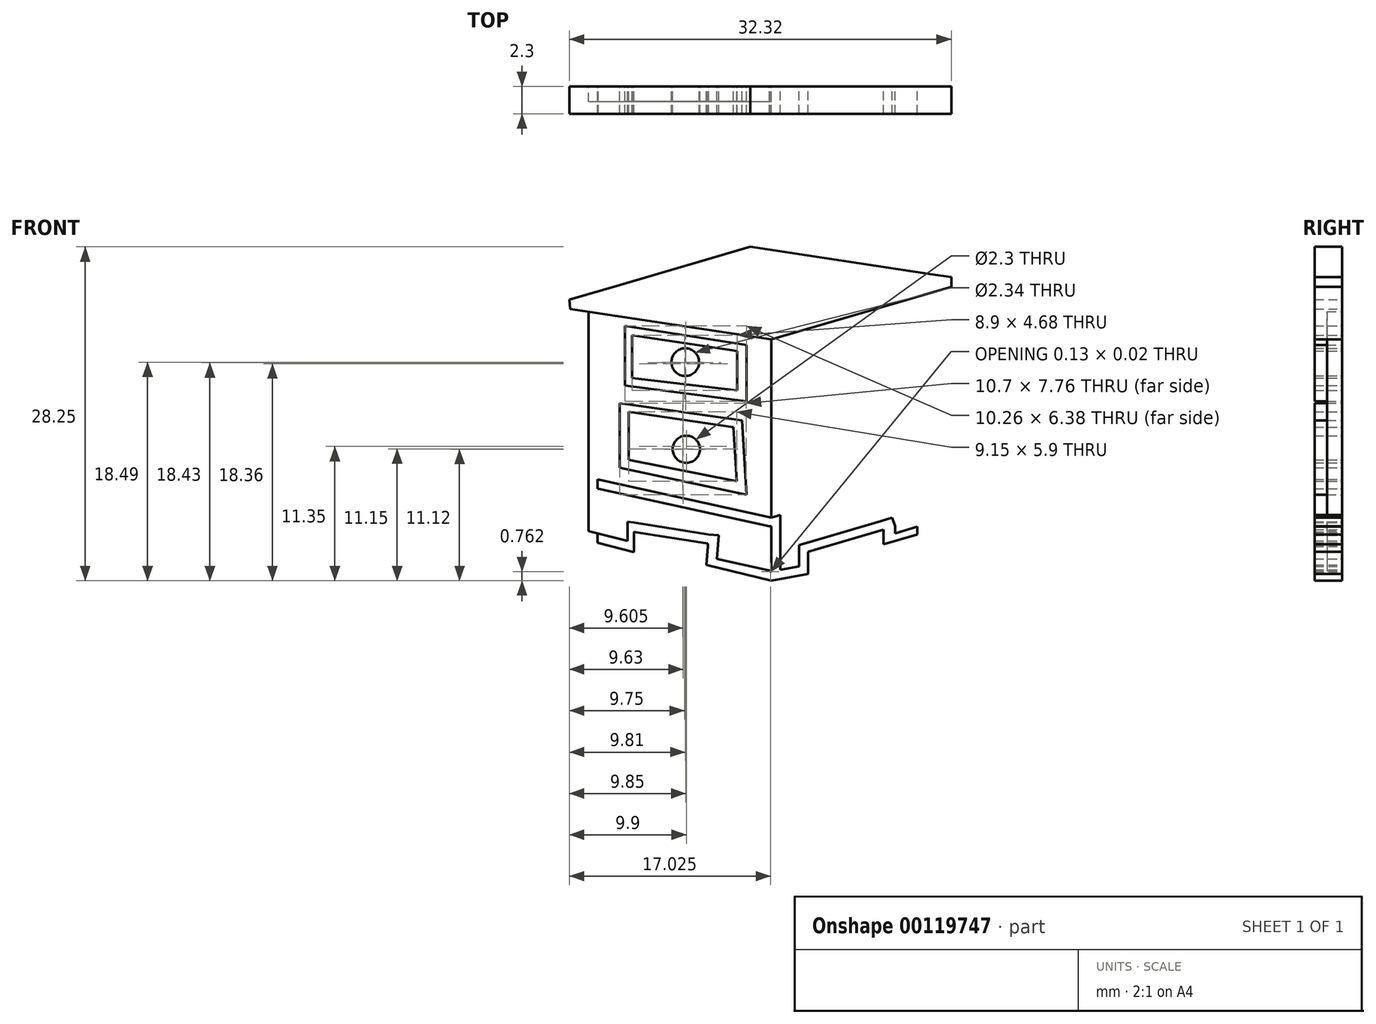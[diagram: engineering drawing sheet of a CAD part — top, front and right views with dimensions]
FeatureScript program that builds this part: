
annotation { "Feature Type Name" : "Feature", "Feature Type Description" : "" }
export const myFeature = defineFeature(function(context is Context, id is Id, definition is map)
    precondition{}
    {
        {
            var Q0;
            Q0=qCreatedBy(makeId("Front.planeOp"),FACE);
            var sketch = newSketch(context, id + "F0", { "sketchPlane" : qUnion([Q0])});
            skLineSegment(sketch, "E0", {"start": v(-15.39, 16.06) * mm, "end": v(-15.39, 1.77) * mm});
            skLineSegment(sketch, "E1", {"start": v(-15.39, 1.77) * mm, "end": v(-3.96, 5.12) * mm});
            skLineSegment(sketch, "E2", {"start": v(-3.96, 5.12) * mm, "end": v(-3.96, 19.54) * mm});
            skLineSegment(sketch, "E3", {"start": v(-32.39, 19.42) * mm, "end": v(-15.39, 16.84) * mm});
            skLineSegment(sketch, "E4", {"start": v(-15.39, 16.84) * mm, "end": v(-0.16, 21.3) * mm});
            skLineSegment(sketch, "E5", {"start": v(-30.1, 18.49) * mm, "end": v(-30.1, 4.99) * mm});
            skLineSegment(sketch, "E6", {"start": v(-17.87, 10) * mm, "end": v(-28.2, 11.46) * mm});
            skLineSegment(sketch, "E7", {"start": v(-28.2, 11.46) * mm, "end": v(-28.2, 5.97) * mm});
            skLineSegment(sketch, "E8", {"start": v(-28.2, 5.97) * mm, "end": v(-17.5, 3.7) * mm});
            skLineSegment(sketch, "E9", {"start": v(-17.5, 3.7) * mm, "end": v(-17.87, 10) * mm});
            skLineSegment(sketch, "E10", {"start": v(-27.76, 17.98) * mm, "end": v(-27.76, 12.93) * mm});
            skLineSegment(sketch, "E11", {"start": v(-27.76, 12.93) * mm, "end": v(-17.5, 11.6) * mm});
            skLineSegment(sketch, "E12", {"start": v(-17.5, 11.6) * mm, "end": v(-17.5, 16.37) * mm});
            skLineSegment(sketch, "E13", {"start": v(-17.5, 16.37) * mm, "end": v(-27.76, 17.98) * mm});
            skLineSegment(sketch, "E14", {"start": v(-30.1, 4.99) * mm, "end": v(-15.39, 1.77) * mm});
            skLineSegment(sketch, "E15", {"start": v(-15.39, 1.77) * mm, "end": v(-15.39, -3.57) * mm});
            skLineSegment(sketch, "E16", {"start": v(-15.39, -3.57) * mm, "end": v(-12.27, -3) * mm});
            skLineSegment(sketch, "E17", {"start": v(-12.27, -3) * mm, "end": v(-12.27, -1.12) * mm});
            skLineSegment(sketch, "E18", {"start": v(-12.27, -1.12) * mm, "end": v(-5.88, 0.75) * mm});
            skLineSegment(sketch, "E19", {"start": v(-5.88, 0.75) * mm, "end": v(-5.88, -0.5) * mm});
            skLineSegment(sketch, "E20", {"start": v(-5.88, -0.5) * mm, "end": v(-3.05, 0.34) * mm});
            skLineSegment(sketch, "E21", {"start": v(-30.86, 4.93) * mm, "end": v(-30.86, -0.16) * mm});
            skLineSegment(sketch, "E22", {"start": v(-30.86, -0.16) * mm, "end": v(-27.01, -1.15) * mm});
            skLineSegment(sketch, "E23", {"start": v(-27.01, -1.15) * mm, "end": v(-27.01, 1.34) * mm});
            skLineSegment(sketch, "E24", {"start": v(-27.01, 1.34) * mm, "end": v(-20.7, 0.35) * mm});
            skLineSegment(sketch, "E25", {"start": v(-20.7, 0.35) * mm, "end": v(-20.87, -2.25) * mm});
            skLineSegment(sketch, "E26", {"start": v(-20.87, -2.25) * mm, "end": v(-15.39, -3.57) * mm});
            skLineSegment(sketch, "E27.0", {"start": v(-14.63, 16.06) * mm, "end": v(-14.63, 1.77) * mm});
            skLineSegment(sketch, "E28.0", {"start": v(-15.17, 1.04) * mm, "end": v(-3.83, 4.36) * mm});
            skLineSegment(sketch, "E29.0", {"start": v(-30.02, 4.2) * mm, "end": v(-15.53, 1.02) * mm});
            skLineSegment(sketch, "E30.0", {"start": v(-30.1, 4.99) * mm, "end": v(-30.1, -0.15) * mm});
            skLineSegment(sketch, "E31.0", {"start": v(-30.85, 0.62) * mm, "end": v(-27, -0.36) * mm});
            skLineSegment(sketch, "E32", {"start": v(-30.85, 0.62) * mm, "end": v(-30.85, 0.62) * mm});
            skLineSegment(sketch, "E33", {"start": v(-30.85, 0.62) * mm, "end": v(-30.86, 0.62) * mm});
            skLineSegment(sketch, "E34", {"start": v(-27, -0.36) * mm, "end": v(-27.01, -0.37) * mm});
            skLineSegment(sketch, "E35", {"start": v(-30.1, -0.15) * mm, "end": v(-30.1, -0.36) * mm});
            skLineSegment(sketch, "E36", {"start": v(-30.02, 4.2) * mm, "end": v(-30.1, 4.2) * mm});
            skLineSegment(sketch, "E37", {"start": v(-30.1, 4.2) * mm, "end": v(-30.09, 4.2) * mm});
            skLineSegment(sketch, "E38", {"start": v(-15.53, 1.02) * mm, "end": v(-15.39, 1.02) * mm});
            skLineSegment(sketch, "E39", {"start": v(-15.39, 1.02) * mm, "end": v(-15.4, 0.96) * mm});
            skLineSegment(sketch, "E40", {"start": v(-15.39, 1.02) * mm, "end": v(-15.17, 1.04) * mm});
            skLineSegment(sketch, "E41", {"start": v(-15.39, 16.06) * mm, "end": v(-15.39, 16.84) * mm});
            skLineSegment(sketch, "E42", {"start": v(-14.63, 16.06) * mm, "end": v(-14.63, 17.06) * mm});
            skLineSegment(sketch, "E43", {"start": v(-14.63, 1.77) * mm, "end": v(-14.63, 1.2) * mm});
            skLineSegment(sketch, "E44.0", {"start": v(-27.05, 0.57) * mm, "end": v(-20.74, -0.42) * mm});
            skLineSegment(sketch, "E45", {"start": v(-27.05, 0.57) * mm, "end": v(-27.01, 0.54) * mm});
            skLineSegment(sketch, "E46", {"start": v(-20.74, -0.42) * mm, "end": v(-20.77, -0.7) * mm});
            skLineSegment(sketch, "E47", {"start": v(-19.84, 0.27) * mm, "end": v(-20.05, -2.45) * mm});
            skLineSegment(sketch, "E48", {"start": v(-19.84, 0.27) * mm, "end": v(-20.7, 0.35) * mm});
            skLineSegment(sketch, "E49", {"start": v(-27.01, 1.34) * mm, "end": v(-27.56, 1.42) * mm});
            skLineSegment(sketch, "E50", {"start": v(-27.56, 1.42) * mm, "end": v(-27.56, -1.01) * mm});
            skLineSegment(sketch, "E51", {"start": v(-20.83, -1.55) * mm, "end": v(-15.39, -2.74) * mm});
            skLineSegment(sketch, "E52", {"start": v(-15.39, -2.74) * mm, "end": v(-15.39, -2.66) * mm});
            skLineSegment(sketch, "E53.0", {"start": v(-14.63, 1.77) * mm, "end": v(-14.63, -3.57) * mm});
            skLineSegment(sketch, "E54", {"start": v(-14.63, -3.57) * mm, "end": v(-14.65, -3.44) * mm});
            skLineSegment(sketch, "E55.0", {"start": v(-15.52, -2.82) * mm, "end": v(-12.4, -2.25) * mm});
            skLineSegment(sketch, "E56.0", {"start": v(-13.03, -3) * mm, "end": v(-13.03, -1.12) * mm});
            skLineSegment(sketch, "E57.0", {"start": v(-12.48, -0.4) * mm, "end": v(-6.1, 1.48) * mm});
            skLineSegment(sketch, "E58", {"start": v(-4.92, 1.03) * mm, "end": v(-4.92, -0.21) * mm});
            skLineSegment(sketch, "E59", {"start": v(-4.92, 1.03) * mm, "end": v(-5.88, 0.75) * mm});
            skLineSegment(sketch, "E60", {"start": v(-6.1, 1.48) * mm, "end": v(-5.16, 1.75) * mm});
            skLineSegment(sketch, "E61", {"start": v(-5.16, 1.75) * mm, "end": v(-4.92, 1.03) * mm});
            skLineSegment(sketch, "E62", {"start": v(-12.48, -0.4) * mm, "end": v(-13.04, -0.56) * mm});
            skLineSegment(sketch, "E63", {"start": v(-13.04, -0.56) * mm, "end": v(-13.03, -1.12) * mm});
            skLineSegment(sketch, "E64", {"start": v(-12.4, -2.25) * mm, "end": v(-12.27, -2.22) * mm});
            skLineSegment(sketch, "E65", {"start": v(-13.03, -3) * mm, "end": v(-13.03, -3.14) * mm});
            skLineSegment(sketch, "E66", {"start": v(-15.52, -2.82) * mm, "end": v(-15.39, -2.82) * mm});
            skLineSegment(sketch, "E67.0", {"start": v(-30.86, 18.49) * mm, "end": v(-30.86, 4.93) * mm});
            skLineSegment(sketch, "E68.0", {"start": v(-32.48, 20.2) * mm, "end": v(-15.47, 17.62) * mm});
            skLineSegment(sketch, "E69", {"start": v(-32.48, 20.2) * mm, "end": v(-32.39, 19.42) * mm});
            skLineSegment(sketch, "E70", {"start": v(-15.47, 17.62) * mm, "end": v(-15.39, 16.84) * mm});
            skLineSegment(sketch, "E71", {"start": v(-30.86, 18.49) * mm, "end": v(-30.86, 19.19) * mm});
            skLineSegment(sketch, "E72", {"start": v(-30.1, 18.49) * mm, "end": v(-30.1, 19.07) * mm});
            skLineSegment(sketch, "E73", {"start": v(-5.04, 0.4) * mm, "end": v(-3.05, 1) * mm});
            skPoint(sketch, "E73.startSnap0", {"position": v(-5.04, 1.39) * mm});
            skPoint(sketch, "E73.startSnap1", {"position": v(-4.92, 0.4) * mm});
            skLineSegment(sketch, "E74", {"start": v(-3.83, 4.36) * mm, "end": v(-3.79, 0.78) * mm});
            skLineSegment(sketch, "E75.0", {"start": v(-3.2, 4.74) * mm, "end": v(-3.2, 19.54) * mm});
            skLineSegment(sketch, "E76", {"start": v(-3.96, 19.54) * mm, "end": v(-3.97, 20.18) * mm});
            skLineSegment(sketch, "E77", {"start": v(-3.2, 19.54) * mm, "end": v(-3.2, 20.4) * mm});
            skLineSegment(sketch, "E78", {"start": v(-15.47, 17.62) * mm, "end": v(-0.16, 22.1) * mm});
            skLineSegment(sketch, "E79", {"start": v(-0.16, 22.1) * mm, "end": v(-0.16, 21.3) * mm});
            skLineSegment(sketch, "E80", {"start": v(-0.16, 22.1) * mm, "end": v(-1.74, 22.34) * mm});
            skLineSegment(sketch, "E81", {"start": v(-32.48, 20.2) * mm, "end": v(-28.18, 21.46) * mm});
            skLineSegment(sketch, "E82", {"start": v(-27.45, 10.73) * mm, "end": v(-27.45, 6.66) * mm});
            skPoint(sketch, "E82.startSnap0", {"position": v(-23.03, 10.73) * mm});
            skLineSegment(sketch, "E83", {"start": v(-27.45, 6.66) * mm, "end": v(-18.3, 4.83) * mm});
            skLineSegment(sketch, "E84", {"start": v(-18.3, 4.83) * mm, "end": v(-18.59, 9.4) * mm});
            skLineSegment(sketch, "E85", {"start": v(-18.59, 9.4) * mm, "end": v(-27.45, 10.73) * mm});
            skLineSegment(sketch, "E86", {"start": v(-27.18, 17.2) * mm, "end": v(-27.18, 13.57) * mm});
            skLineSegment(sketch, "E87", {"start": v(-27.18, 13.57) * mm, "end": v(-18.28, 12.52) * mm});
            skLineSegment(sketch, "E88", {"start": v(-18.28, 12.52) * mm, "end": v(-18.28, 15.86) * mm});
            skLineSegment(sketch, "E89", {"start": v(-18.28, 15.86) * mm, "end": v(-27.18, 17.2) * mm});
            skCircle(sketch, "E90", {"center": v(-22.58, 7.55) * mm, "radius": 1.15 * mm});
            skCircle(sketch, "E91", {"center": v(-22.67, 14.92) * mm, "radius": 1.17 * mm});
            skLineSegment(sketch, "E92", {"start": v(-28.18, 21.46) * mm, "end": v(-17.16, 24.68) * mm});
            skLineSegment(sketch, "E93", {"start": v(-1.74, 22.34) * mm, "end": v(-17.16, 24.68) * mm});
            skLineSegment(sketch, "E94", {"start": v(-17.11, 23.9) * mm, "end": v(-30.7, 19.93) * mm});
            skLineSegment(sketch, "E95", {"start": v(-17.11, 23.9) * mm, "end": v(-1.9, 21.6) * mm});
            skLineSegment(sketch, "E96", {"start": v(-3.05, 0.34) * mm, "end": v(-3.05, 1) * mm});
            skLineSegment(sketch, "E97", {"start": v(-3.05, 1) * mm, "end": v(-3.2, 4.74) * mm});
            skSolve(sketch);
        }
        {
            var Q0;
            Q0=makeQuery(id+"F0.imprint","IMPRINT",FACE,{"disambiguationData":[TD([[makeQuery(id+"F0.imprint","IMPRINT",EDGE,{"derivedFrom":sQuery(id+"F0.wireOp",EDGE,"E0")}),-1.0]])]});
            var Q1;
            Q1=makeQuery(id+"F0.imprint","IMPRINT",FACE,{"disambiguationData":[TD([[makeQuery(id+"F0.imprint","IMPRINT",EDGE,{"derivedFrom":sQuery(id+"F0.wireOp",EDGE,"E86")}),1.0]])]});
            var Q2;
            {var subQ3=sQuery(id+"F0.wireOp",EDGE,"E94");Q2=makeQuery(id+"F0.imprint","IMPRINT",FACE,{"disambiguationData":[TD([[makeQuery(id+"F0.imprint","IMPRINT",EDGE,{"derivedFrom":subQ3}),1.0]])]});}
            var Q3;
            {var subQ6=sQuery(id+"F0.wireOp",EDGE,"E2");Q3=makeQuery(id+"F0.imprint","IMPRINT",FACE,{"disambiguationData":[TD([[makeQuery(id+"F0.imprint","IMPRINT",EDGE,{"derivedFrom":subQ6}),1.0]])]});}
            var Q4;
            Q4=makeQuery(id+"F0.imprint","IMPRINT",FACE,{"disambiguationData":[TD([[makeQuery(id+"F0.imprint","IMPRINT",EDGE,{"derivedFrom":sQuery(id+"F0.wireOp",EDGE,"E57.0")}),1.0]])]});
            var Q5;
            Q5=makeQuery(id+"F0.imprint","IMPRINT",FACE,{"disambiguationData":[TD([[makeQuery(id+"F0.imprint","IMPRINT",EDGE,{"derivedFrom":sQuery(id+"F0.wireOp",EDGE,"E24")}),1.0]])]});
            var Q6;
            Q6=makeQuery(id+"F0.imprint","IMPRINT",FACE,{"disambiguationData":[TD([[makeQuery(id+"F0.imprint","IMPRINT",EDGE,{"derivedFrom":sQuery(id+"F0.wireOp",EDGE,"E82")}),1.0]])]});
            extrude(context, id + "F1", {"entities" : qUnion([Q0, Q1, Q2, Q3, Q4, Q5, Q6]), "depth" : 1.27 * mm});
        }
        {
            var Q0;
            {var subQ0=sQuery(id+"F0.wireOp",EDGE,"E69");Q0=makeQuery(id+"F0.imprint","IMPRINT",FACE,{"disambiguationData":[TD([[makeQuery(id+"F0.imprint","IMPRINT",EDGE,{"derivedFrom":subQ0}),1.0]])]});}
            var Q1;
            {var subQ11=sQuery(id+"F0.wireOp",EDGE,"E5");Q1=makeQuery(id+"F0.imprint","IMPRINT",FACE,{"disambiguationData":[TD([[makeQuery(id+"F0.imprint","IMPRINT",EDGE,{"derivedFrom":subQ11}),-1.0]])]});}
            var Q2;
            {var subQ1=sQuery(id+"F0.wireOp",EDGE,"E14");Q2=makeQuery(id+"F0.imprint","IMPRINT",FACE,{"disambiguationData":[TD([[makeQuery(id+"F0.imprint","IMPRINT",EDGE,{"derivedFrom":subQ1}),-1.0]])]});}
            var Q3;
            {var subQ0=sQuery(id+"F0.wireOp",EDGE,"E32");Q3=makeQuery(id+"F0.imprint","IMPRINT",FACE,{"disambiguationData":[TD([[makeQuery(id+"F0.imprint","IMPRINT",EDGE,{"derivedFrom":subQ0}),1.0]])]});}
            var Q4;
            {var subQ5=sQuery(id+"F0.wireOp",EDGE,"E35");Q4=makeQuery(id+"F0.imprint","IMPRINT",FACE,{"disambiguationData":[TD([[makeQuery(id+"F0.imprint","IMPRINT",EDGE,{"derivedFrom":subQ5}),1.0]])]});}
            var Q5;
            {var subQ1=sQuery(id+"F0.wireOp",EDGE,"E23");var subQ6=sQuery(id+"F0.wireOp",EDGE,"E22");var subQ7=makeQuery(id+"F0.imprint","INTERSECT",VERTEX,{"derivedFrom":[subQ6,subQ1]});Q5=makeQuery(id+"F0.imprint","IMPRINT",FACE,{"disambiguationData":[TD([[makeQuery(id+"F0.imprint","IMPRINT",EDGE,{"disambiguationData":[TD([[subQ7,1.0]])],"derivedFrom":subQ6}),1.0]])]});}
            var Q6;
            {var subQ8=sQuery(id+"F0.wireOp",EDGE,"E45");Q6=makeQuery(id+"F0.imprint","IMPRINT",FACE,{"disambiguationData":[TD([[makeQuery(id+"F0.imprint","IMPRINT",EDGE,{"derivedFrom":subQ8}),-1.0]])]});}
            var Q7;
            {var subQ0=sQuery(id+"F0.wireOp",EDGE,"E24");Q7=makeQuery(id+"F0.imprint","IMPRINT",FACE,{"disambiguationData":[TD([[makeQuery(id+"F0.imprint","IMPRINT",EDGE,{"derivedFrom":subQ0}),-1.0]])]});}
            var Q8;
            {var subQ0=sQuery(id+"F0.wireOp",EDGE,"E46");Q8=makeQuery(id+"F0.imprint","IMPRINT",FACE,{"disambiguationData":[TD([[makeQuery(id+"F0.imprint","IMPRINT",EDGE,{"derivedFrom":subQ0}),1.0]])]});}
            var Q9;
            {var subQ0=sQuery(id+"F0.wireOp",EDGE,"E26");var subQ1=sQuery(id+"F0.wireOp",EDGE,"E25");var subQ2=makeQuery(id+"F0.imprint","INTERSECT",VERTEX,{"derivedFrom":[subQ1,subQ0]});Q9=makeQuery(id+"F0.imprint","IMPRINT",FACE,{"disambiguationData":[TD([[makeQuery(id+"F0.imprint","IMPRINT",EDGE,{"disambiguationData":[TD([[subQ2,1.0]])],"derivedFrom":subQ1}),1.0]])]});}
            var Q10;
            {var subQ7=sQuery(id+"F0.wireOp",EDGE,"E66");Q10=makeQuery(id+"F0.imprint","IMPRINT",FACE,{"disambiguationData":[TD([[makeQuery(id+"F0.imprint","IMPRINT",EDGE,{"derivedFrom":subQ7}),-1.0]])]});}
            var Q11;
            {var subQ6=sQuery(id+"F0.wireOp",EDGE,"E15");var subQ8=makeQuery(id+"F0.imprint","INTERSECT",VERTEX,{"derivedFrom":[subQ6,sQuery(id+"F0.wireOp",EDGE,"E66")]});Q11=makeQuery(id+"F0.imprint","IMPRINT",FACE,{"disambiguationData":[TD([[makeQuery(id+"F0.imprint","IMPRINT",EDGE,{"disambiguationData":[TD([[subQ8,1.0]])],"derivedFrom":subQ6}),1.0]])]});}
            var Q12;
            {var subQ0=sQuery(id+"F0.wireOp",EDGE,"E40");Q12=makeQuery(id+"F0.imprint","IMPRINT",FACE,{"disambiguationData":[TD([[makeQuery(id+"F0.imprint","IMPRINT",EDGE,{"derivedFrom":subQ0}),-1.0]])]});}
            var Q13;
            {var subQ3=sQuery(id+"F0.wireOp",EDGE,"E40");Q13=makeQuery(id+"F0.imprint","IMPRINT",FACE,{"disambiguationData":[TD([[makeQuery(id+"F0.imprint","IMPRINT",EDGE,{"derivedFrom":subQ3}),1.0]])]});}
            var Q14;
            {var subQ0=sQuery(id+"F0.wireOp",EDGE,"E65");Q14=makeQuery(id+"F0.imprint","IMPRINT",FACE,{"disambiguationData":[TD([[makeQuery(id+"F0.imprint","IMPRINT",EDGE,{"derivedFrom":subQ0}),-1.0]])]});}
            var Q15;
            {var subQ4=sQuery(id+"F0.wireOp",EDGE,"E64");Q15=makeQuery(id+"F0.imprint","IMPRINT",FACE,{"disambiguationData":[TD([[makeQuery(id+"F0.imprint","IMPRINT",EDGE,{"derivedFrom":subQ4}),-1.0]])]});}
            var Q16;
            {var subQ1=sQuery(id+"F0.wireOp",EDGE,"E18");Q16=makeQuery(id+"F0.imprint","IMPRINT",FACE,{"disambiguationData":[TD([[makeQuery(id+"F0.imprint","IMPRINT",EDGE,{"derivedFrom":subQ1}),1.0]])]});}
            var Q17;
            {var subQ1=sQuery(id+"F0.wireOp",EDGE,"E19");Q17=makeQuery(id+"F0.imprint","IMPRINT",FACE,{"disambiguationData":[TD([[makeQuery(id+"F0.imprint","IMPRINT",EDGE,{"derivedFrom":subQ1}),1.0]])]});}
            var Q18;
            {var subQ6=sQuery(id+"F0.wireOp",EDGE,"E96");Q18=makeQuery(id+"F0.imprint","IMPRINT",FACE,{"disambiguationData":[TD([[makeQuery(id+"F0.imprint","IMPRINT",EDGE,{"derivedFrom":subQ6}),1.0]])]});}
            var Q19;
            {var subQ2=sQuery(id+"F0.wireOp",EDGE,"E2");Q19=makeQuery(id+"F0.imprint","IMPRINT",FACE,{"disambiguationData":[TD([[makeQuery(id+"F0.imprint","IMPRINT",EDGE,{"derivedFrom":subQ2}),-1.0]])]});}
            var Q20;
            {var subQ6=sQuery(id+"F0.wireOp",EDGE,"E0");Q20=makeQuery(id+"F0.imprint","IMPRINT",FACE,{"disambiguationData":[TD([[makeQuery(id+"F0.imprint","IMPRINT",EDGE,{"derivedFrom":subQ6}),1.0]])]});}
            var Q21;
            {var subQ5=sQuery(id+"F0.wireOp",EDGE,"E70");Q21=makeQuery(id+"F0.imprint","IMPRINT",FACE,{"disambiguationData":[TD([[makeQuery(id+"F0.imprint","IMPRINT",EDGE,{"derivedFrom":subQ5}),1.0]])]});}
            var Q22;
            {var subQ0=sQuery(id+"F0.wireOp",EDGE,"E80");Q22=makeQuery(id+"F0.imprint","IMPRINT",FACE,{"disambiguationData":[TD([[makeQuery(id+"F0.imprint","IMPRINT",EDGE,{"derivedFrom":subQ0}),1.0]])]});}
            var Q23;
            Q23=makeQuery(id+"F0.imprint","IMPRINT",FACE,{"disambiguationData":[TD([[makeQuery(id+"F0.imprint","IMPRINT",EDGE,{"derivedFrom":sQuery(id+"F0.wireOp",EDGE,"E91")}),1.0]])]});
            var Q24;
            Q24=makeQuery(id+"F0.imprint","IMPRINT",FACE,{"disambiguationData":[TD([[makeQuery(id+"F0.imprint","IMPRINT",EDGE,{"derivedFrom":sQuery(id+"F0.wireOp",EDGE,"E10")}),1.0]])]});
            var Q25;
            Q25=makeQuery(id+"F0.imprint","IMPRINT",FACE,{"disambiguationData":[TD([[makeQuery(id+"F0.imprint","IMPRINT",EDGE,{"derivedFrom":sQuery(id+"F0.wireOp",EDGE,"E6")}),1.0]])]});
            var Q26;
            Q26=makeQuery(id+"F0.imprint","IMPRINT",FACE,{"disambiguationData":[TD([[makeQuery(id+"F0.imprint","IMPRINT",EDGE,{"derivedFrom":sQuery(id+"F0.wireOp",EDGE,"E90")}),1.0]])]});
            extrude(context, id + "F2", {"entities" : qUnion([Q0, Q1, Q2, Q3, Q4, Q5, Q6, Q7, Q8, Q9, Q10, Q11, Q12, Q13, Q14, Q15, Q16, Q17, Q18, Q19, Q20, Q21, Q22, Q23, Q24, Q25, Q26]), "depth" : 2.3 * mm});
        }
    });
